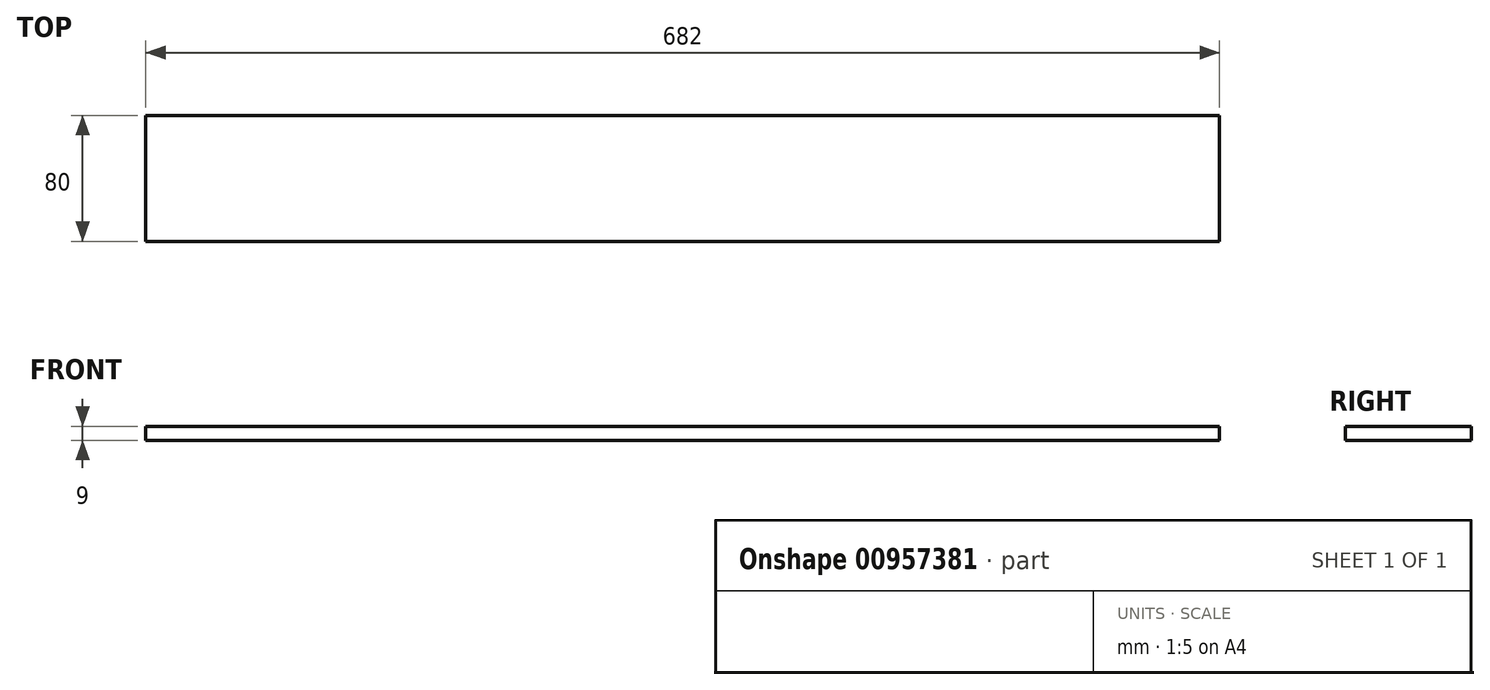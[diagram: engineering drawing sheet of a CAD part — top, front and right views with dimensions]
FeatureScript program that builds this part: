
annotation { "Feature Type Name" : "Feature", "Feature Type Description" : "" }
export const myFeature = defineFeature(function(context is Context, id is Id, definition is map)
    precondition{}
    {
        {
            var Q0;
            Q0=qCreatedBy(makeId("Top.planeOp"),FACE);
            var sketch = newSketch(context, id + "F0", { "sketchPlane" : qUnion([Q0])});
            skLineSegment(sketch, "E0.bottom", {"start": v(341, 40) * mm, "end": v(-341, 40) * mm});
            skLineSegment(sketch, "E0.top", {"start": v(341, -40) * mm, "end": v(-341, -40) * mm});
            skLineSegment(sketch, "E0.left", {"start": v(341, 40) * mm, "end": v(341, -40) * mm});
            skLineSegment(sketch, "E0.right", {"start": v(-341, 40) * mm, "end": v(-341, -40) * mm});
            skPoint(sketch, "E0.middle", {"position": v(0, 0) * mm});
            skSolve(sketch);
        }
        {
            var Q0;
            Q0=makeQuery(id+"F0.imprint","IMPRINT",FACE,{"disambiguationData":[TD([[makeQuery(id+"F0.imprint","IMPRINT",EDGE,{"derivedFrom":sQuery(id+"F0.wireOp",EDGE,"E0.bottom")}),1.0]])]});
            extrude(context, id + "F1", {"entities" : qUnion([Q0]), "depth" : 9 * mm, "offsetDistance" : 25 * mm});
        }
    });
